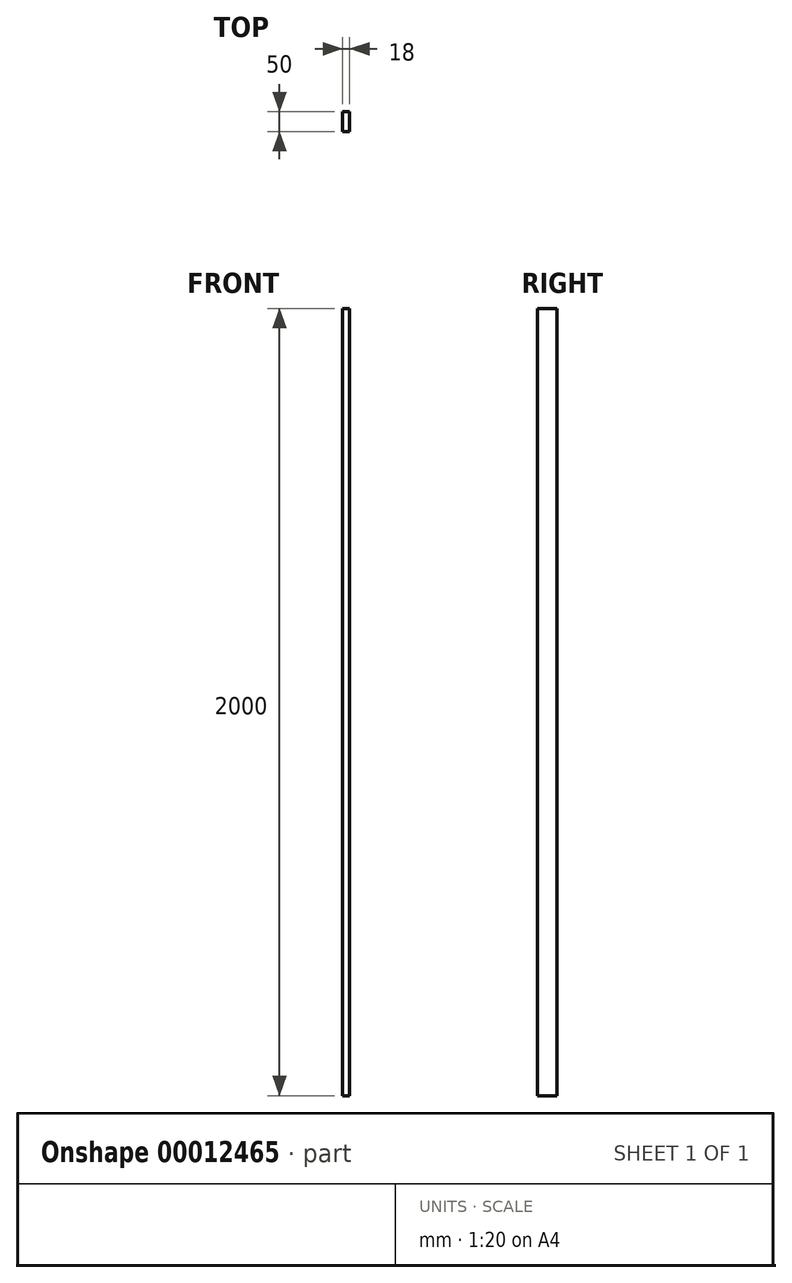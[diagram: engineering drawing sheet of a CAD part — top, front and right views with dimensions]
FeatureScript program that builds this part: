
annotation { "Feature Type Name" : "Feature", "Feature Type Description" : "" }
export const myFeature = defineFeature(function(context is Context, id is Id, definition is map)
    precondition{}
    {
        {
            var Q0;
            Q0=qCreatedBy(makeId("Top.planeOp"),FACE);
            var sketch = newSketch(context, id + "F0", { "sketchPlane" : qUnion([Q0])});
            skLineSegment(sketch, "E0.rect.bottom", {"start": v(-9, 25) * mm, "end": v(9, 25) * mm});
            skLineSegment(sketch, "E0.rect.top", {"start": v(-9, -25) * mm, "end": v(9, -25) * mm});
            skLineSegment(sketch, "E0.rect.left", {"start": v(-9, 25) * mm, "end": v(-9, -25) * mm});
            skLineSegment(sketch, "E0.rect.right", {"start": v(9, 25) * mm, "end": v(9, -25) * mm});
            skPoint(sketch, "E0.rect.middle", {"position": v(0, 0) * mm});
            skSolve(sketch);
        }
        {
            var Q0;
            Q0=makeQuery(id+"F0.imprint","IMPRINT",FACE,{"disambiguationData":[TD([[makeQuery(id+"F0.imprint","IMPRINT",EDGE,{"derivedFrom":sQuery(id+"F0.wireOp",EDGE,"E0.rect.bottom")}),-1.0]])]});
            extrude(context, id + "F1", {"entities" : qUnion([Q0]), "depth" : 2000 * mm});
        }
    });
